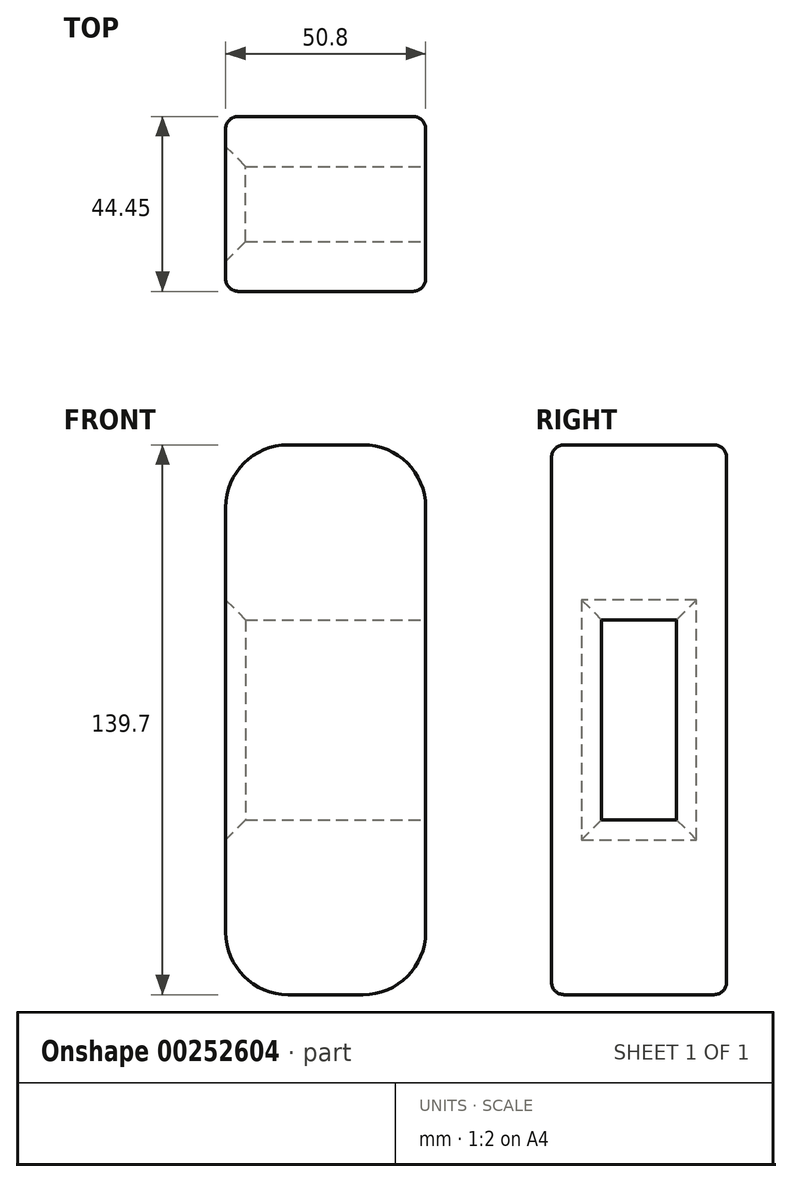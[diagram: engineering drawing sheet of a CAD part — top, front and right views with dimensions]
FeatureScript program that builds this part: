
annotation { "Feature Type Name" : "Feature", "Feature Type Description" : "" }
export const myFeature = defineFeature(function(context is Context, id is Id, definition is map)
    precondition{}
    {
        {
            var Q0;
            Q0=qCreatedBy(makeId("Front.planeOp"),FACE);
            var sketch = newSketch(context, id + "F0", { "sketchPlane" : qUnion([Q0])});
            skLineSegment(sketch, "E0.bottom", {"start": v(9.53, 69.85) * mm, "end": v(-9.53, 69.85) * mm});
            skLineSegment(sketch, "E0.top", {"start": v(9.52, -69.85) * mm, "end": v(-9.52, -69.85) * mm});
            skLineSegment(sketch, "E0.left", {"start": v(25.4, 53.98) * mm, "end": v(25.4, -53.97) * mm});
            skLineSegment(sketch, "E0.right", {"start": v(-25.4, 53.98) * mm, "end": v(-25.4, -53.97) * mm});
            skPoint(sketch, "E0.middle", {"position": v(0, 0) * mm});
            skPoint(sketch, "E1.visualSharp", {"position": v(-25.4, 69.85) * mm});
            skArc(sketch, "E1.filletArc", {"start": v(-9.53, 69.85) * mm, "mid": v(-20.75, 65.2) * mm, "end": v(-25.4, 53.98) * mm});
            skPoint(sketch, "E2.visualSharp", {"position": v(25.4, 69.85) * mm});
            skArc(sketch, "E2.filletArc", {"start": v(25.4, 53.98) * mm, "mid": v(20.75, 65.2) * mm, "end": v(9.53, 69.85) * mm});
            skPoint(sketch, "E3.visualSharp", {"position": v(-25.4, -69.85) * mm});
            skArc(sketch, "E3.filletArc", {"start": v(-25.4, -53.97) * mm, "mid": v(-20.75, -65.2) * mm, "end": v(-9.53, -69.85) * mm});
            skPoint(sketch, "E4.visualSharp", {"position": v(25.4, -69.85) * mm});
            skArc(sketch, "E4.filletArc", {"start": v(9.53, -69.85) * mm, "mid": v(20.75, -65.2) * mm, "end": v(25.4, -53.97) * mm});
            skSolve(sketch);
        }
        {
            var Q0;
            Q0=makeQuery(id+"F0.imprint","IMPRINT",FACE,{"disambiguationData":[TD([[makeQuery(id+"F0.imprint","IMPRINT",EDGE,{"derivedFrom":sQuery(id+"F0.wireOp",EDGE,"E0.bottom")}),1.0]])]});
            extrude(context, id + "F1", {"entities" : qUnion([Q0]), "depth" : 44.45 * mm});
        }
        {
            var Q0;
            Q0=makeQuery(id+"F1.opExtrude","CAP_FACE",FACE,{"disambiguationData":[OSD([sQuery(id+"F0.wireOp",EDGE,"E0.bottom"),sQuery(id+"F0.wireOp",EDGE,"E0.top"),sQuery(id+"F0.wireOp",EDGE,"E0.left"),sQuery(id+"F0.wireOp",EDGE,"E0.right"),sQuery(id+"F0.wireOp",EDGE,"E1.filletArc"),sQuery(id+"F0.wireOp",EDGE,"E2.filletArc"),sQuery(id+"F0.wireOp",EDGE,"E3.filletArc"),sQuery(id+"F0.wireOp",EDGE,"E4.filletArc")])],"isStart":false});
            var Q1;
            Q1=makeQuery(id+"F1.opExtrude","CAP_FACE",FACE,{"disambiguationData":[OSD([sQuery(id+"F0.wireOp",EDGE,"E0.bottom"),sQuery(id+"F0.wireOp",EDGE,"E0.top"),sQuery(id+"F0.wireOp",EDGE,"E0.left"),sQuery(id+"F0.wireOp",EDGE,"E0.right"),sQuery(id+"F0.wireOp",EDGE,"E1.filletArc"),sQuery(id+"F0.wireOp",EDGE,"E2.filletArc"),sQuery(id+"F0.wireOp",EDGE,"E3.filletArc"),sQuery(id+"F0.wireOp",EDGE,"E4.filletArc")])],"isStart":true});
            fillet(context, id + "F2", {"entities" : qUnion([Q0, Q1]), "radius" : 3.17 * mm, "tangentPropagation" : true, "allowEdgeOverflow" : false});
        }
        {
            var Q0;
            Q0=makeQuery(id+"F1.opExtrude","SWEPT_FACE",FACE,{"disambiguationData":[OSD([sQuery(id+"F0.wireOp",EDGE,"E0.left")])]});
            var sketch = newSketch(context, id + "F3", { "sketchPlane" : qUnion([Q0])});
            skPoint(sketch, "E5.endSnap0", {"position": v(-3.18, 0) * mm});
            skLineSegment(sketch, "E6.bottom", {"start": v(-12.7, 25.4) * mm, "end": v(-31.75, 25.4) * mm});
            skLineSegment(sketch, "E6.top", {"start": v(-12.7, -25.4) * mm, "end": v(-31.75, -25.4) * mm});
            skLineSegment(sketch, "E6.left", {"start": v(-12.7, 25.4) * mm, "end": v(-12.7, -25.4) * mm});
            skLineSegment(sketch, "E6.right", {"start": v(-31.75, 25.4) * mm, "end": v(-31.75, -25.4) * mm});
            skPoint(sketch, "E6.middle", {"position": v(-22.23, 0) * mm});
            skSolve(sketch);
        }
        {
            var Q0;
            Q0=makeQuery(id+"F3.imprint","IMPRINT",FACE,{"disambiguationData":[TD([[makeQuery(id+"F3.imprint","IMPRINT",EDGE,{"derivedFrom":sQuery(id+"F3.wireOp",EDGE,"E6.bottom")}),1.0]])]});
            extrude(context, id + "F4", {"entities" : qUnion([Q0]), "operationType" : NewBodyOperationType.REMOVE, "endBound" : BoundingType.THROUGH_ALL, "oppositeDirection" : true, "depth" : 25.4 * mm});
        }
        {
            var Q0;
            Q0=makeQuery(id+"F4.boolean.opBoolean","COPY",EDGE,{"derivedFrom":makeQuery(id+"F4.opExtrude","CAP_EDGE",EDGE,{"disambiguationData":[OSD([sQuery(id+"F3.wireOp",EDGE,"E6.right")])],"isStart":true})});
            var Q1;
            Q1=makeQuery(id+"F4.boolean.opBoolean","COPY",EDGE,{"derivedFrom":makeQuery(id+"F4.opExtrude","CAP_EDGE",EDGE,{"disambiguationData":[OSD([sQuery(id+"F3.wireOp",EDGE,"E6.bottom")])],"isStart":true})});
            var Q2;
            Q2=makeQuery(id+"F4.boolean.opBoolean","COPY",EDGE,{"derivedFrom":makeQuery(id+"F4.opExtrude","CAP_EDGE",EDGE,{"disambiguationData":[OSD([sQuery(id+"F3.wireOp",EDGE,"E6.left")])],"isStart":true})});
            var Q3;
            Q3=makeQuery(id+"F4.boolean.opBoolean","COPY",EDGE,{"derivedFrom":makeQuery(id+"F4.opExtrude","CAP_EDGE",EDGE,{"disambiguationData":[OSD([sQuery(id+"F3.wireOp",EDGE,"E6.top")])],"isStart":true})});
            var Q4;
            Q4=makeQuery(id+"F4.boolean.opBoolean","INTERSECT",EDGE,{"derivedFrom":[makeQuery(id+"F1.opExtrude","SWEPT_FACE",FACE,{"disambiguationData":[OSD([sQuery(id+"F0.wireOp",EDGE,"E0.right")])]}),makeQuery(id+"F4.opExtrude","SWEPT_FACE",FACE,{"disambiguationData":[OSD([sQuery(id+"F3.wireOp",EDGE,"E6.bottom")])]})]});
            var Q5;
            Q5=makeQuery(id+"F4.boolean.opBoolean","INTERSECT",EDGE,{"derivedFrom":[makeQuery(id+"F1.opExtrude","SWEPT_FACE",FACE,{"disambiguationData":[OSD([sQuery(id+"F0.wireOp",EDGE,"E0.right")])]}),makeQuery(id+"F4.opExtrude","SWEPT_FACE",FACE,{"disambiguationData":[OSD([sQuery(id+"F3.wireOp",EDGE,"E6.right")])]})]});
            var Q6;
            Q6=makeQuery(id+"F4.boolean.opBoolean","INTERSECT",EDGE,{"derivedFrom":[makeQuery(id+"F1.opExtrude","SWEPT_FACE",FACE,{"disambiguationData":[OSD([sQuery(id+"F0.wireOp",EDGE,"E0.right")])]}),makeQuery(id+"F4.opExtrude","SWEPT_FACE",FACE,{"disambiguationData":[OSD([sQuery(id+"F3.wireOp",EDGE,"E6.top")])]})]});
            var Q7;
            Q7=makeQuery(id+"F4.boolean.opBoolean","INTERSECT",EDGE,{"derivedFrom":[makeQuery(id+"F1.opExtrude","SWEPT_FACE",FACE,{"disambiguationData":[OSD([sQuery(id+"F0.wireOp",EDGE,"E0.right")])]}),makeQuery(id+"F4.opExtrude","SWEPT_FACE",FACE,{"disambiguationData":[OSD([sQuery(id+"F3.wireOp",EDGE,"E6.left")])]})]});
            chamfer(context, id + "F5", {"entities" : qUnion([Q0, Q1, Q2, Q3, Q4, Q5, Q6, Q7]), "width" : 5.08 * mm, "tangentPropagation" : true});
        }
    });
